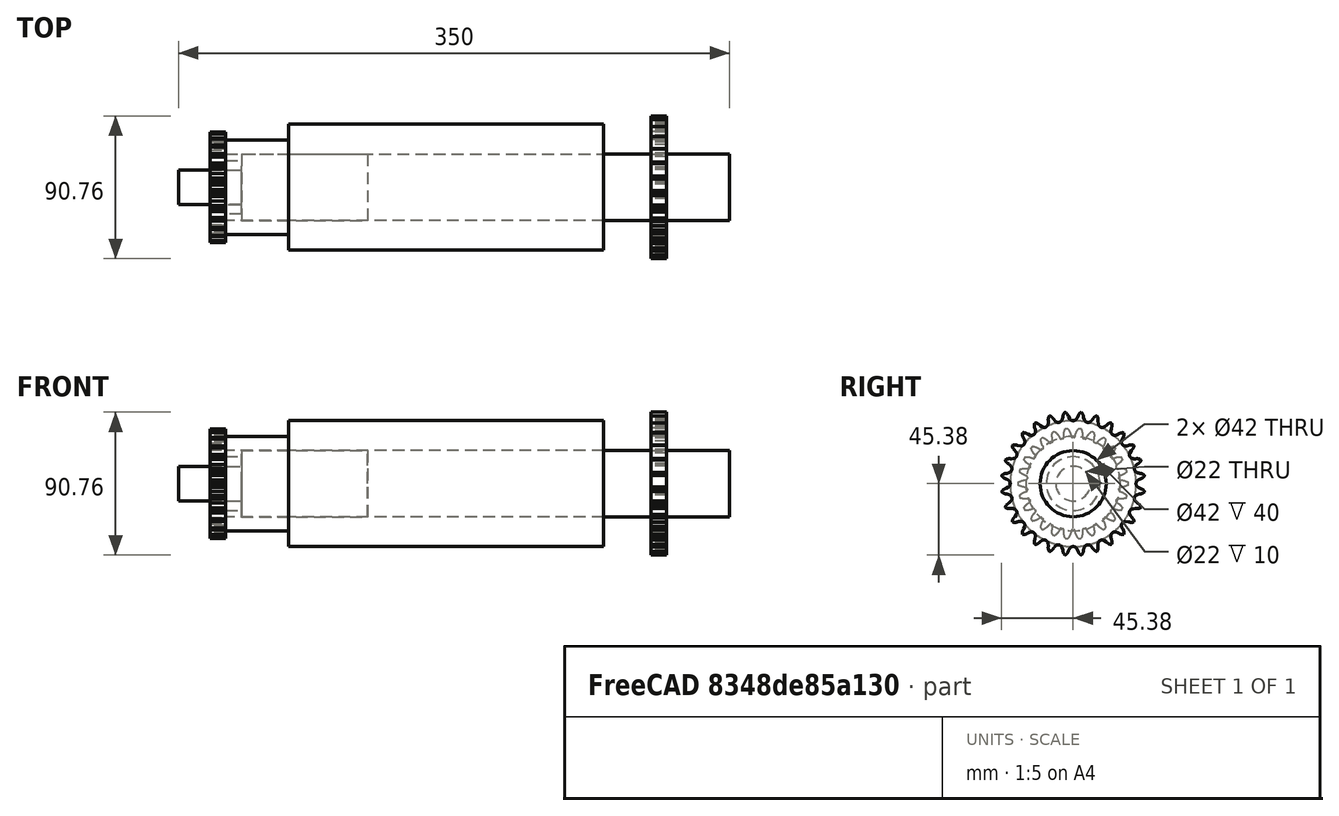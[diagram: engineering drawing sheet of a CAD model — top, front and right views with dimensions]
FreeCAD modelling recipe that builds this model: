
FCSTD DOCUMENT  (FreeCAD 0.20R29603 (Git))
Label: Machine Components Design
License: All rights reserved
LicenseURL: http://en.wikipedia.org/wiki/All_rights_reserved
objects: Sketcher::SketchObject×13, PartDesign::Body×8, PartDesign::Pad×6, Part::Part2DObjectPython×2, App::Part×2, PartDesign::Revolution×1, Fem::ConstraintFixed×1, Fem::ConstraintForce×1, PartDesign::Hole×1, PartDesign::Pocket×1
note: 41 computed .brp shape members not serialized (recipe doc carries the construction recipe); baked Part::Feature solids carry a one-line shape summary decoded from their .brp

FEATURE [Sketcher::SketchObject] Sketch
  FullyConstrained = false
  MapMode = 5
  Placement = pos=(0,0,0) rot=(1,0,0;1.5708rad)
  Support = -> [XZ_Plane]
  sketch-geometry (2):
    g0: Circle CenterX=0 CenterY=0 CenterZ=0 NormalX=0 NormalY=0 NormalZ=1 AngleXU=0 Radius=17.1233
    g1: Circle CenterX=0 CenterY=0 CenterZ=0 NormalX=0 NormalY=0 NormalZ=1 AngleXU=0 Radius=11
  constraints (3):
    c: Coincident(g0,g-1)
    c: Coincident(g1,g0)
    c: Diameter(g1) = 22
FEATURE [PartDesign::Pad] Pad
  Direction = (0,-1,-2e-16)
  Length = 10
  Length2 = 10
  Placement = pos=(0,0,0) rot=(1,0,0;1.5708rad)
  Profile = -> Sketch
  ReferenceAxis = -> Sketch [N_Axis]
  Type = 0
FEATURE [Sketcher::SketchObject] Sketch001
  FullyConstrained = true
  MapMode = 5
  Placement = pos=(0,0,0) rot=(1,0,0;1.5708rad)
  Support = -> [XZ_Plane]
FEATURE [PartDesign::Body] Body
  Group = -> [Sketch,Pad,Sketch001]
  Origin = -> Origin
  Placement = pos=(40,-4e-15,0) rot=(0,0,-1;1.5708rad)
  Tip = -> Pad
FEATURE [Sketcher::SketchObject] Sketch002
  FullyConstrained = true
  MapMode = 5
  Placement = pos=(0,0,0) rot=(1,0,0;1.5708rad)
  Support = -> [XZ_Plane001]
FEATURE [Sketcher::SketchObject] SketchShaft
  FullyConstrained = true
  MapMode = 5
  Support = -> [XY_Plane003]
  sketch-geometry (6):
    g0: LineSegment StartX=0 StartY=0 StartZ=0 EndX=120 EndY=0 EndZ=0
    g1: LineSegment StartX=0 StartY=0 StartZ=0 EndX=0 EndY=11 EndZ=0
    g2: LineSegment StartX=0 StartY=11 StartZ=0 EndX=40 EndY=11 EndZ=0
    g3: LineSegment StartX=40 StartY=11 StartZ=0 EndX=40 EndY=21 EndZ=0
    g4: LineSegment StartX=40 StartY=21 StartZ=0 EndX=120 EndY=21 EndZ=0
    g5: LineSegment StartX=120 StartY=21 StartZ=0 EndX=120 EndY=0 EndZ=0
  constraints (18):
    c: DistanceX(g0) = 120
    c: DistanceY(g-1,g0) = 0
    c: PointOnObject(g0,g-2)
    c: Horizontal(g0)
    c: DistanceY(g-1,g1) = 11
    c: Coincident(g0,g1)
    c: Vertical(g1)
    c: DistanceX(g2) = 40
    c: Coincident(g2,g1)
    c: Horizontal(g2)
    c: DistanceY(g-1,g3) = 21
    c: Coincident(g3,g2)
    c: Vertical(g3)
    c: DistanceX(g4) = 80
    c: Coincident(g4,g3)
    c: Horizontal(g4)
    c: Coincident(g0,g5)
    c: Coincident(g5,g4)
FEATURE [PartDesign::Revolution] RevolutionShaft
  Angle = 360
  Axis = (1,0,0)
  Base = (0,0,0)
  Profile = -> SketchShaft
  ReferenceAxis = -> SketchShaft [H_Axis]
FEATURE [Fem::ConstraintFixed] ShaftConstraintFixed
  NormalDirection = (1,0,0)
  Normals = (4) [(1,0,0),(1,0,0),(1,0,0),(1,0,0)]
  Points = (4) [(120,-7,-7),(120,7,-7),(120,-7,7),(120,7,7)]
  References = -> [RevolutionShaft]
  Scale = 5
FEATURE [Fem::ConstraintForce] ShaftConstraintForce
  DirectionVector = (0,0,1)
  Force = 1000
  NormalDirection = (0,0,1)
FEATURE [Part::Part2DObjectPython] InvoluteGear  # Draft 2D object (typed FeaturePython)
  ExternalGear = true
  HighPrecision = true
  Modules = 2.5
  NumberOfTeeth = 26
  PressureAngle = 20
FEATURE [PartDesign::Pad] Pad002
  Direction = (0,0,1)
  Length = 10
  Length2 = 10
  Profile = -> InvoluteGear
  ReferenceAxis = -> InvoluteGear [N_Axis]
  Type = 0
FEATURE [PartDesign::Body] RevolutionShaftBody
  Group = -> [SketchShaft,RevolutionShaft]
  Origin = -> Origin003
  Tip = -> RevolutionShaft
FEATURE [Sketcher::SketchObject] Sketch003
  FullyConstrained = true
  MapMode = 5
  Placement = pos=(0,0,10) rot=(0,0,1;0rad)
  Support = -> [Pad002]
  sketch-geometry (1):
    g0: Circle CenterX=0 CenterY=0 CenterZ=0 NormalX=0 NormalY=0 NormalZ=1 AngleXU=0 Radius=11
  constraints (2):
    c: Coincident(g0,g-1)
    c: Diameter(g0) = 22
FEATURE [PartDesign::Hole] Hole
  BaseFeature = -> Pad002
  CustomThreadClearance = 0
  Depth = 25
  DepthType = 0
  Diameter = 22
  DrillForDepth = false
  DrillPoint = 1
  DrillPointAngle = 118
  HoleCutCountersinkAngle = 90
  HoleCutCustomValues = false
  HoleCutDepth = 0
  HoleCutDiameter = 6.1
  HoleCutType = 0
  ModelThread = false
  Profile = -> Sketch003
  Tapered = false
  TaperedAngle = 90
  ThreadClass = 0
  ThreadDepth = 25
  ThreadDepthType = 0
  ThreadDirection = 0
  ThreadFit = 0
  ThreadSize = 0
  ThreadType = 0
  Threaded = false
  UseCustomThreadClearance = false
FEATURE [Sketcher::SketchObject] Sketch004
  FullyConstrained = true
  MapMode = 5
  Support = -> [XY_Plane001]
FEATURE [Sketcher::SketchObject] Sketch006
  FullyConstrained = false
  MapMode = 5
  Placement = pos=(0,0,0) rot=(0.57735,0.57735,0.57735;2.0944rad)
  Support = -> [YZ_Plane004]
  sketch-geometry (2):
    g0: Circle CenterX=0 CenterY=0 CenterZ=0 NormalX=0 NormalY=0 NormalZ=1 AngleXU=0 Radius=21
    g1: Circle CenterX=0 CenterY=0 CenterZ=0 NormalX=0 NormalY=0 NormalZ=1 AngleXU=0 Radius=40
  constraints (2):
    c: Diameter(g0) = 42
    c: Diameter(g1) = 80
FEATURE [PartDesign::Pad] Pad003
  Direction = (1,-2e-16,3e-16)
  Length = 200
  Length2 = 10
  Placement = pos=(0,0,0) rot=(0.57735,0.57735,0.57735;2.0944rad)
  Profile = -> Sketch006
  ReferenceAxis = -> Sketch006 [N_Axis]
  Type = 0
FEATURE [Sketcher::SketchObject] Sketch007
  FullyConstrained = true
  MapMode = 5
  Placement = pos=(0,0,0) rot=(0.57735,0.57735,0.57735;2.0944rad)
  Support = -> [YZ_Plane005]
FEATURE [PartDesign::Body] Body003
  Group = -> [Sketch007]
  Origin = -> Origin005
FEATURE [App::Part] Part
  Group = -> [RevolutionShaftBody,Body003]
  Origin = -> Origin002
FEATURE [App::Part] Part001
  Origin = -> Origin006
FEATURE [Sketcher::SketchObject] Sketch008
  FullyConstrained = true
  MapMode = 5
  Support = -> [XY_Plane001]
  sketch-geometry (1):
    g0: Circle CenterX=0 CenterY=0 CenterZ=0 NormalX=0 NormalY=0 NormalZ=1 AngleXU=0 Radius=10.5
  constraints (2):
    c: Coincident(g0,g-1)
    c: Diameter(g0) = 21
FEATURE [PartDesign::Body] Body001
  Group = -> [Sketch002,InvoluteGear,Pad002,Sketch003,Hole,Sketch004,Sketch008]
  Origin = -> Origin001
  Placement = pos=(30,-1.6e-14,4e-15) rot=(0.57735,-0.57735,-0.57735;2.0944rad)
  Tip = -> Hole
FEATURE [Sketcher::SketchObject] Sketch009
  FullyConstrained = true
  MapMode = 5
  Placement = pos=(0,0,0) rot=(0.57735,0.57735,0.57735;2.0944rad)
  Support = -> [YZ_Plane004]
FEATURE [PartDesign::Body] Body002
  Group = -> [Sketch006,Pad003,Sketch009]
  Origin = -> Origin004
  Placement = pos=(70,0,0) rot=(0,0,1;0rad)
  Tip = -> Pad003
FEATURE [Sketcher::SketchObject] Sketch010
  FullyConstrained = false
  MapMode = 5
  Placement = pos=(0,0,0) rot=(0.57735,0.57735,0.57735;2.0944rad)
  Support = -> [YZ_Plane007]
  sketch-geometry (1):
    g0: Circle CenterX=0 CenterY=0 CenterZ=0 NormalX=0 NormalY=0 NormalZ=1 AngleXU=0 Radius=21
  constraints (1):
    c: Diameter(g0) = 42
FEATURE [PartDesign::Pad] Pad004
  Direction = (1,-2e-16,3e-16)
  Length = 80
  Length2 = 10
  Placement = pos=(0,0,0) rot=(0.57735,0.57735,0.57735;2.0944rad)
  Profile = -> Sketch010
  ReferenceAxis = -> Sketch010 [N_Axis]
  Type = 0
FEATURE [PartDesign::Body] Body004
  Group = -> [Sketch010,Pad004]
  Origin = -> Origin007
  Placement = pos=(270,0,0) rot=(0,0,1;0rad)
  Tip = -> Pad004
FEATURE [Part::Part2DObjectPython] Sprocket  # Draft 2D object (typed FeaturePython)
  NumberOfTeeth = 28
  Pitch = 9.525
  RollerDiameter = 5.08
  SprocketReference = 1
  Thickness = 4.27
FEATURE [PartDesign::Pad] Pad005
  Direction = (0,0,1)
  Length = 10
  Length2 = 10
  Profile = -> Sprocket
  ReferenceAxis = -> Sprocket [N_Axis]
  Type = 0
FEATURE [Sketcher::SketchObject] Sketch011
  FullyConstrained = false
  MapMode = 5
  Support = -> [XY_Plane008]
  sketch-geometry (1):
    g0: Circle CenterX=0 CenterY=0 CenterZ=0 NormalX=0 NormalY=0 NormalZ=1 AngleXU=0 Radius=21
  constraints (1):
    c: Diameter(g0) = 42
FEATURE [PartDesign::Pocket] Pocket
  BaseFeature = -> Pad005
  Direction = (0,0,-1)
  Length = 20
  Length2 = 5
  Midplane = true
  Profile = -> Sketch011
  ReferenceAxis = -> Sketch011 [N_Axis]
  Type = 0
FEATURE [PartDesign::Body] Body005
  Group = -> [Sprocket,Pad005,Sketch011,Pocket]
  Origin = -> Origin008
  Placement = pos=(310,0,-1.11e-14) rot=(0,1,0;4.71239rad)
  Tip = -> Pocket
FEATURE [Sketcher::SketchObject] Sketch012
  FullyConstrained = false
  MapMode = 5
  Placement = pos=(0,0,0) rot=(0.57735,0.57735,0.57735;2.0944rad)
  Support = -> [YZ_Plane009]
  sketch-geometry (2):
    g0: Circle CenterX=0 CenterY=0 CenterZ=0 NormalX=0 NormalY=0 NormalZ=1 AngleXU=0 Radius=30
    g1: Circle CenterX=0 CenterY=0 CenterZ=0 NormalX=0 NormalY=0 NormalZ=1 AngleXU=0 Radius=21
  constraints (3):
    c: Coincident(g0,g-1)
    c: Diameter(g1) = 42
    c: Diameter(g0) = 60
FEATURE [PartDesign::Pad] Pad006
  Direction = (1,-2e-16,3e-16)
  Length = 40
  Length2 = 10
  Placement = pos=(0,0,0) rot=(0.57735,0.57735,0.57735;2.0944rad)
  Profile = -> Sketch012
  ReferenceAxis = -> Sketch012 [N_Axis]
  Type = 0
FEATURE [PartDesign::Body] Body006
  Group = -> [Sketch012,Pad006]
  Origin = -> Origin009
  Placement = pos=(30,0,0) rot=(0,0,1;0rad)
  Tip = -> Pad006
